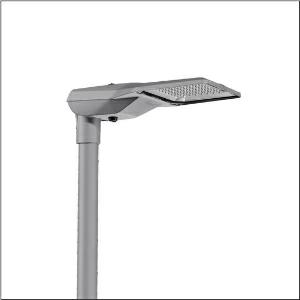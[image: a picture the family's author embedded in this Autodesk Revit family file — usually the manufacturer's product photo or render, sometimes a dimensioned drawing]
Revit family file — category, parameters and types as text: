
# Revit family: streetlight_sl_21_iq_midi___st1_0a_5xe3d31y08nb_4ee3
name_source: partatom
category: Lighting Fixtures
units: mm (PartAtom-declared; Revit-internal decimal feet)

## family parameters
Cut with Voids When Loaded = No
Host = Face
Light Source = No
Part Type = Normal
Room Calculation Point = No
Round Connector Dimension = Use Diameter
Shared = No

## types (1)
- --- (1 x LED, 21550 lm, 136.6 W, 3000K)
    Apparent Load = 137 VA
    CIE Flux Codes = 40 73 97 100 100
    Color Rendering = 70
    Color Temperature = 3000K
    Default Elevation = 1800 mm
    Description = Streetlight SL 21 iQ midi, mast luminaire, primary light control with lens, of PMMA, primary optical cover: cover, of toughened safety glass, transparent, light distribution: ST1.0a, light emission: direct distribution, primary light characteristic: asymmetric, installation type: post-top, side-entry, LED, High Power LED, rated luminous flux: 21.550lm, luminous efficacy: 158lm/W, light colour: 730, colour temperature: 3000K, control: presetting dimming logarithmic, Street-Remote, Auto-Match, Temp-Guard, Lumen-Switch, Night-Set, Smart-Wire, Light-Fading, Desk-Remote (wireless, voltage-free reading and setting of iQ features in the workshop via application-optimized NFC function/RFID function), optimised constant luminous flux control (CLO 2.0), mains connection: 230..240V, AC, 50/60Hz, start of lifetime: 137W, end of service life: 144W, reduction: 61W, luminaire housing, of diecast aluminium, powder-coated, Siteco® metallic grey (DB 702S), corrosivity category C5 mid according to DIN EN ISO 12944, please order mast flange separately, inclination adjustable: 0°, 5°, 10°, 15°, sealing non-destructively replaceable, multi-level sealing system, length: 644mm, width: 335mm, height: 110mm, mast flange for spigot size: 42mm (side-entry): 5XC10008XM4, 60/48mm (side-entry/post-top): 5XC10108XM2, 76/60mm (side-entry/post-top): 5XC10108XM1, Smart Interface below and above, protection rating (complete): IP66, insulation class (complete): insulation class II (safety insulation), certification: CE, ENEC, ENEC+, VDE, impact resistance: IK09, permissible operating ambient temperature for outdoor applications: -40..+50°C, standard-compliant lighting for roads and squares, packaging unit: 1 piece

Light Distribution: ST1.0a
    Height = 111 mm
    Lamp = 1 x LED
    Lamp Light Flux = 21550 lm
    Lamp Power = 136.6 W
    Lamp count = 1
    Length = 644 mm
    Luminous efficacy = 158 lm/W
    Manufacturer = Siteco
    ModVariant = No
    Model = 5XE3D31Y08NB
    Number of Poles = 1
    OnlyDefault = Yes
    Power Factor = 1
    Product Name = Streetlight SL 21 iQ midi | ST1.0a
    Product group = mast luminaire | pylon top
    ProductGroupID = 6100
    Protection Class = Protection class II
    Protection Degree = IP 66
    RLX_Detail_Level = 1
    RLX_Emergency_Light_Flux = 0 lm
    RLX_Emergency_Type = 0
    RLX_Emergency_Type_DB = No
    RlxData = <blob elided: 91905 chars, md5=1e289608>
    Socket = socket
    Standby Power = 0 W
    System Light Flux = 21550 lm
    System Power = 137 W
    Type Comments = factory setting: luminous flux: 100 % | dim-lin: 254 | 733 mA
    Type Image = l_1004304.jpg
    URL = http://relux.com
    VarID = @adj_062003
    Voltage = 0 V
    Weight = 0.00 kg
    Width = 336 mm

## geometry (parser evidence)
native form markers: Blend x4, Sweep x11
no freeform markers — native parametric forms only
